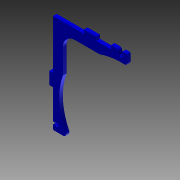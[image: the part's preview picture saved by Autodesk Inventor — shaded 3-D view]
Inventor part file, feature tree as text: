
AUTODESK INVENTOR PART (.ipt)
format: ipt  version: 2012 (Build 160160000, 160)  size: 145,408 bytes
history: native  units: mm
features: extrude x1, sketch x1
ambient origin geometry x8: Origin, YZ Plane, XZ Plane, XY Plane, X Axis, Y Axis, Z Axis, Center Point
feature tree (2):
  extrude  "Extrusion3"  Depth=10.0mm
  sketch  "Sketch2"  dims[d0=100.0mm d5=10.0mm d6=10.0mm d13=40.0mm d14=25.0mm d15=3.0mm d16=3.0mm d17=3.0mm d18=3.0mm d22=55.0mm d23=55.0mm d31=3.0mm d33=135.0deg d34=45.0deg d35=135.0deg d36=45.0deg d37=3.0mm d43=12.0mm d44=3.0mm d46=3.0mm d48=3.0mm d50=45.0deg d51=135.0deg d53=2.0mm d54=1.0mm d57=80.0mm d58=3.0mm d59=5.0mm d60=3.0mm d61=3.0mm d62=135.0deg d63=45.0deg d64=1.0mm d65=2.0mm d66=1.0mm d67=3.0mm d75=4.050253mm d76=60.0mm d78=5.0mm d79=3.0mm d85=3.0mm d86=0.0mm d87=60.0deg d92=8.0mm d93=50.0mm d94=50.0mm d95=8.0mm d96=10.0mm d97=2.0mm d98=2.0mm]
